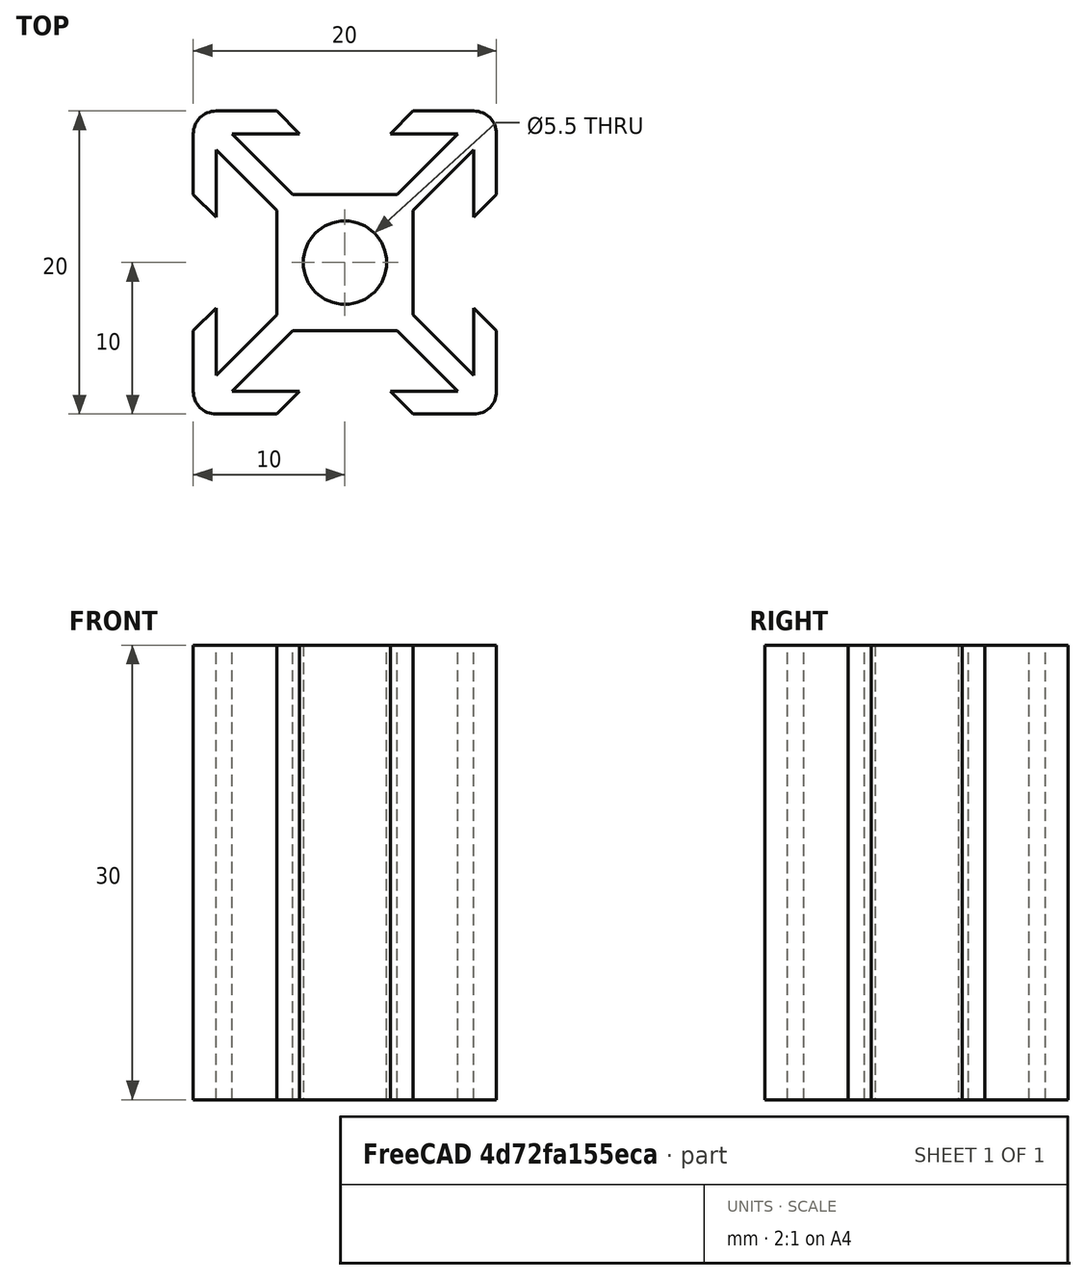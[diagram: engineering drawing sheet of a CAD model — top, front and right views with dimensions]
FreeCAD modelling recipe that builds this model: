
FCSTD DOCUMENT  (FreeCAD 0.20R29603 (Git))
Label: normal_beam_2020
License: All rights reserved
LicenseURL: http://en.wikipedia.org/wiki/All_rights_reserved
objects: Spreadsheet::Sheet×1, Sketcher::SketchObject×1, PartDesign::Pad×1, PartDesign::Body×1
note: 4 computed .brp shape members not serialized (recipe doc carries the construction recipe); baked Part::Feature solids carry a one-line shape summary decoded from their .brp

FEATURE [Spreadsheet::Sheet] Spreadsheet  label="parameters"
  cells = A1=Beam dimensions; A2=Length; B2(beam_length)=30
FEATURE [Sketcher::SketchObject] Sketch
  FullyConstrained = true
  MapMode = 5
  Support = -> [XY_Plane]
  sketch-geometry (57):
    g0: Circle CenterX=0 CenterY=0 CenterZ=0 NormalX=0 NormalY=0 NormalZ=1 AngleXU=0 Radius=2.75
    g1: LineSegment StartX=-4.5 StartY=4.5 StartZ=0 EndX=4.5 EndY=4.5 EndZ=0
    g2: LineSegment StartX=4.5 StartY=4.5 StartZ=0 EndX=4.5 EndY=-4.5 EndZ=0
    g3: LineSegment StartX=4.5 StartY=-4.5 StartZ=0 EndX=-4.5 EndY=-4.5 EndZ=0
    g4: LineSegment StartX=-4.5 StartY=-4.5 StartZ=0 EndX=-4.5 EndY=4.5 EndZ=0
    g5: LineSegment StartX=-10 StartY=10 StartZ=0 EndX=10 EndY=10 EndZ=0
    g6: LineSegment StartX=10 StartY=10 StartZ=0 EndX=10 EndY=-10 EndZ=0
    g7: LineSegment StartX=10 StartY=-10 StartZ=0 EndX=-10 EndY=-10 EndZ=0
    g8: LineSegment StartX=-10 StartY=-10 StartZ=0 EndX=-10 EndY=10 EndZ=0
    g9: LineSegment StartX=-8.5 StartY=8.5 StartZ=0 EndX=8.5 EndY=8.5 EndZ=0
    g10: LineSegment StartX=8.5 StartY=8.5 StartZ=0 EndX=8.5 EndY=-8.5 EndZ=0
    g11: LineSegment StartX=8.5 StartY=-8.5 StartZ=0 EndX=-8.5 EndY=-8.5 EndZ=0
    g12: LineSegment StartX=-8.5 StartY=-8.5 StartZ=0 EndX=-8.5 EndY=8.5 EndZ=0
    g13: ArcOfCircle CenterX=-8.5 CenterY=8.5 CenterZ=0 NormalX=0 NormalY=0 NormalZ=1 AngleXU=0 Radius=1.5 StartAngle=1.5708 EndAngle=3.14159
    g14: ArcOfCircle CenterX=8.5 CenterY=8.5 CenterZ=0 NormalX=0 NormalY=0 NormalZ=1 AngleXU=0 Radius=1.5 StartAngle=2.20881e-08 EndAngle=1.5708
    g15: ArcOfCircle CenterX=8.5 CenterY=-8.5 CenterZ=0 NormalX=0 NormalY=0 NormalZ=1 AngleXU=0 Radius=1.5 StartAngle=4.71239 EndAngle=6.28319
    g16: ArcOfCircle CenterX=-8.5 CenterY=-8.5 CenterZ=0 NormalX=0 NormalY=0 NormalZ=1 AngleXU=0 Radius=1.5 StartAngle=3.14159 EndAngle=4.71239
    g17: LineSegment StartX=7.43934 StartY=8.5 StartZ=0 EndX=8.5 EndY=7.43934 EndZ=0
    g18: LineSegment StartX=8.5 StartY=10 StartZ=0 EndX=4.5 EndY=10 EndZ=0
    g19: LineSegment StartX=4.5 StartY=10 StartZ=0 EndX=3 EndY=8.5 EndZ=0
    g20: LineSegment StartX=3 StartY=8.5 StartZ=0 EndX=7.43934 EndY=8.5 EndZ=0
    g21: LineSegment StartX=7.43934 StartY=8.5 StartZ=0 EndX=3.43934 EndY=4.5 EndZ=0
    g22: LineSegment StartX=-8.5 StartY=10 StartZ=0 EndX=-4.5 EndY=10 EndZ=0
    g23: LineSegment StartX=-4.5 StartY=10 StartZ=0 EndX=-3 EndY=8.5 EndZ=0
    g24: LineSegment StartX=-7.43934 StartY=8.5 StartZ=0 EndX=-8.5 EndY=7.43934 EndZ=0
    g25: LineSegment StartX=-8.5 StartY=-7.43934 StartZ=0 EndX=-7.43934 EndY=-8.5 EndZ=0
    g26: LineSegment StartX=8.5 StartY=-7.43934 StartZ=0 EndX=7.43934 EndY=-8.5 EndZ=0
    g27: LineSegment StartX=-3 StartY=8.5 StartZ=0 EndX=-7.43934 EndY=8.5 EndZ=0
    g28: LineSegment StartX=-7.43934 StartY=8.5 StartZ=0 EndX=-3.43934 EndY=4.5 EndZ=0
    g29: LineSegment StartX=-3.43934 StartY=4.5 StartZ=0 EndX=3.43934 EndY=4.5 EndZ=0
    g30: LineSegment StartX=-10 StartY=8.5 StartZ=0 EndX=-10 EndY=4.5 EndZ=0
    g31: LineSegment StartX=-10 StartY=4.5 StartZ=0 EndX=-8.5 EndY=3 EndZ=0
    g32: LineSegment StartX=-8.5 StartY=3 StartZ=0 EndX=-8.5 EndY=7.43934 EndZ=0
    g33: LineSegment StartX=-8.5 StartY=7.43934 StartZ=0 EndX=-4.5 EndY=3.43934 EndZ=0
    g34: LineSegment StartX=-4.5 StartY=3.43934 StartZ=0 EndX=-4.5 EndY=-3.43934 EndZ=0
    g35: LineSegment StartX=-4.5 StartY=-3.43934 StartZ=0 EndX=-8.5 EndY=-7.43934 EndZ=0
    g36: LineSegment StartX=-8.5 StartY=-7.43934 StartZ=0 EndX=-8.5 EndY=-3 EndZ=0
    g37: LineSegment StartX=-8.5 StartY=-3 StartZ=0 EndX=-10 EndY=-4.5 EndZ=0
    g38: LineSegment StartX=-10 StartY=-4.5 StartZ=0 EndX=-10 EndY=-8.5 EndZ=0
    g39: LineSegment StartX=-8.5 StartY=-10 StartZ=0 EndX=-4.5 EndY=-10 EndZ=0
    g40: LineSegment StartX=-4.5 StartY=-10 StartZ=0 EndX=-3 EndY=-8.5 EndZ=0
    g41: LineSegment StartX=-3 StartY=-8.5 StartZ=0 EndX=-7.43934 EndY=-8.5 EndZ=0
    g42: LineSegment StartX=-7.43934 StartY=-8.5 StartZ=0 EndX=-3.43934 EndY=-4.5 EndZ=0
    g43: LineSegment StartX=-3.43934 StartY=-4.5 StartZ=0 EndX=3.43934 EndY=-4.5 EndZ=0
    g44: LineSegment StartX=3.43934 StartY=-4.5 StartZ=0 EndX=7.43934 EndY=-8.5 EndZ=0
    g45: LineSegment StartX=7.43934 StartY=-8.5 StartZ=0 EndX=3 EndY=-8.5 EndZ=0
    g46: LineSegment StartX=3 StartY=-8.5 StartZ=0 EndX=4.5 EndY=-10 EndZ=0
    g47: LineSegment StartX=4.5 StartY=-10 StartZ=0 EndX=8.5 EndY=-10 EndZ=0
    g48: LineSegment StartX=10 StartY=-8.5 StartZ=0 EndX=10 EndY=-4.5 EndZ=0
    g49: LineSegment StartX=10 StartY=-4.5 StartZ=0 EndX=8.5 EndY=-3 EndZ=0
    g50: LineSegment StartX=8.5 StartY=-3 StartZ=0 EndX=8.5 EndY=-7.43934 EndZ=0
    g51: LineSegment StartX=8.5 StartY=-7.43934 StartZ=0 EndX=4.5 EndY=-3.43934 EndZ=0
    g52: LineSegment StartX=4.5 StartY=-3.43934 StartZ=0 EndX=4.5 EndY=3.43934 EndZ=0
    g53: LineSegment StartX=4.5 StartY=3.43934 StartZ=0 EndX=8.5 EndY=7.43934 EndZ=0
    g54: LineSegment StartX=8.5 StartY=7.43934 StartZ=0 EndX=8.5 EndY=3 EndZ=0
    g55: LineSegment StartX=8.5 StartY=3 StartZ=0 EndX=10 EndY=4.5 EndZ=0
    g56: LineSegment StartX=10 StartY=4.5 StartZ=0 EndX=10 EndY=8.5 EndZ=0
  constraints (158):
    c: Coincident(g0,g-1)
    c: Coincident(g1,g2)
    c: Coincident(g2,g3)
    c: Coincident(g3,g4)
    c: Coincident(g4,g1)
    c: Horizontal(g1)
    c: Horizontal(g3)
    c: Vertical(g2)
    c: Vertical(g4)
    c: Symmetric(g1,g3,g0)
    c: Diameter(g0) = 5.5
    c: Equal(g1,g2)
    c: Distance(g1) = 9
    c: Coincident(g5,g6)
    c: Coincident(g6,g7)
    c: Coincident(g7,g8)
    c: Coincident(g8,g5)
    c: Horizontal(g5)
    c: Horizontal(g7)
    c: Vertical(g6)
    c: Vertical(g8)
    c: Symmetric(g5,g7,g0)
    c: Distance(g5) = 20
    c: Equal(g5,g6)
    c: Coincident(g9,g10)
    c: Coincident(g10,g11)
    c: Coincident(g11,g12)
    c: Coincident(g12,g9)
    c: Horizontal(g9)
    c: Horizontal(g11)
    c: Vertical(g10)
    c: Vertical(g12)
    c: Symmetric(g9,g11,g0)
    c: Distance(g9) = 17
    c: Equal(g9,g10)
    c: Coincident(g13,g9)
    c: PointOnObject(g13,g5)
    c: PointOnObject(g13,g8)
    c: Vertical(g13,g13)
    c: Coincident(g14,g9)
    c: PointOnObject(g14,g5)
    c: PointOnObject(g14,g6)
    c: Vertical(g14,g14)
    c: Coincident(g15,g10)
    c: PointOnObject(g15,g6)
    c: PointOnObject(g15,g7)
    c: Vertical(g15,g15)
    c: Coincident(g16,g11)
    c: PointOnObject(g16,g7)
    c: PointOnObject(g16,g8)
    c: Vertical(g16,g16)
    c: PointOnObject(g17,g9)
    c: PointOnObject(g17,g10)
    c: Distance(g17) = 1.5
    c: Angle(g17,g10) = 2.35619
    c: Tangent(g14,g18) = -1.5708
    c: Coincident(g18,g19)
    c: PointOnObject(g19,g9)
    c: Coincident(g19,g20)
    c: Coincident(g20,g17)
    c: Coincident(g20,g21)
    c: PointOnObject(g21,g1)
    c: Angle(g19,g18) = 2.35619
    c: Tangent(g13,g22) = 1.5708
    c: Coincident(g22,g23)
    c: PointOnObject(g23,g9)
    c: PointOnObject(g24,g9)
    c: PointOnObject(g24,g12)
    c: PointOnObject(g25,g12)
    c: PointOnObject(g25,g11)
    c: PointOnObject(g26,g10)
    c: PointOnObject(g26,g11)
    c: Equal(g24,g17)
    c: Equal(g17,g25)
    c: Equal(g17,g26)
    c: Horizontal(g24,g17)
    c: Vertical(g20,g26)
    c: Horizontal(g26,g25)
    c: Coincident(g23,g27)
    c: Coincident(g27,g24)
    c: Coincident(g27,g28)
    c: PointOnObject(g28,g1)
    c: Distance(g19,g23) = 6
    c: Angle(g22,g23) = 2.35619
    c: Equal(g27,g20)
    c: Angle(g20,g21) = 0.785398
    c: Equal(g21,g28)
    c: Coincident(g29,g28)
    c: Coincident(g29,g21)
    c: Tangent(g13,g30) = -1.5708
    c: Coincident(g30,g31)
    c: PointOnObject(g31,g12)
    c: Coincident(g31,g32)
    c: Coincident(g32,g24)
    c: Coincident(g32,g33)
    c: PointOnObject(g33,g4)
    c: Coincident(g33,g34)
    c: PointOnObject(g34,g4)
    c: Coincident(g34,g35)
    c: Coincident(g35,g25)
    c: Coincident(g35,g36)
    c: PointOnObject(g36,g12)
    c: Coincident(g36,g37)
    c: PointOnObject(g37,g8)
    c: Coincident(g37,g38)
    c: Coincident(g38,g16)
    c: Tangent(g16,g39) = -1.5708
    c: Coincident(g39,g40)
    c: PointOnObject(g40,g11)
    c: Coincident(g40,g41)
    c: Coincident(g41,g25)
    c: Coincident(g41,g42)
    c: PointOnObject(g42,g3)
    c: Coincident(g42,g43)
    c: PointOnObject(g43,g3)
    c: Coincident(g43,g44)
    c: Coincident(g44,g26)
    c: Coincident(g44,g45)
    c: PointOnObject(g45,g11)
    c: Coincident(g45,g46)
    c: PointOnObject(g46,g7)
    c: Coincident(g46,g47)
    c: Coincident(g47,g15)
    c: Tangent(g15,g48) = -1.5708
    c: Coincident(g48,g49)
    c: PointOnObject(g49,g10)
    c: Coincident(g49,g50)
    c: Coincident(g50,g26)
    c: Coincident(g50,g51)
    c: PointOnObject(g51,g2)
    c: Coincident(g51,g52)
    c: PointOnObject(g52,g2)
    c: Coincident(g52,g53)
    c: Coincident(g53,g17)
    c: Coincident(g53,g54)
    c: PointOnObject(g54,g10)
    c: Coincident(g54,g55)
    c: PointOnObject(g55,g6)
    c: Coincident(g55,g56)
    c: Coincident(g56,g14)
    c: Equal(g21,g53)
    c: Equal(g21,g51)
    c: Equal(g21,g44)
    c: Equal(g21,g42)
    c: Equal(g21,g35)
    c: Equal(g20,g32)
    c: Equal(g20,g36)
    c: Equal(g20,g41)
    c: Vertical(g22,g39)
    c: Vertical(g18,g46)
    c: Equal(g20,g45)
    c: Equal(g21,g33)
    c: Angle(g31,g30) = 2.35619
    c: Angle(g38,g37) = 2.35619
    c: Horizontal(g31,g54)
    c: Horizontal(g30,g55)
    c: Horizontal(g36,g49)
    c: Horizontal(g37,g48)
FEATURE [PartDesign::Pad] Pad  label="extrusion_body"
  Direction = (0,0,1)
  Length = 30
  Length2 = 10
  Profile = -> Sketch
  ReferenceAxis = -> Sketch [N_Axis]
  Type = 0
  expr: Length = <<parameters>>.beam_length
FEATURE [PartDesign::Body] Body
  Group = -> [Sketch,Pad]
  Origin = -> Origin
  Tip = -> Pad
